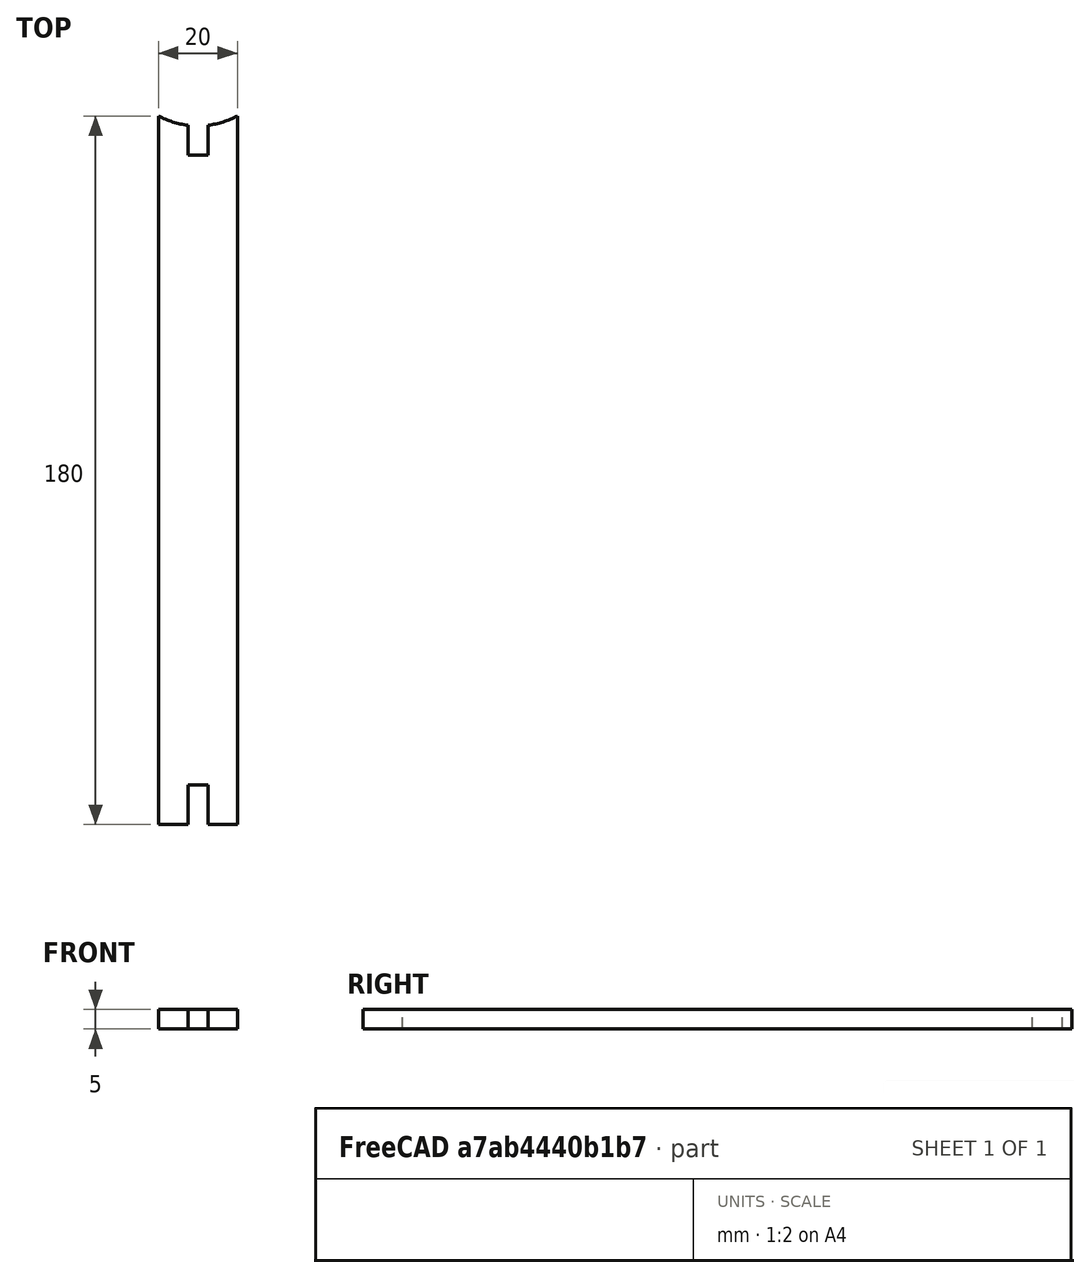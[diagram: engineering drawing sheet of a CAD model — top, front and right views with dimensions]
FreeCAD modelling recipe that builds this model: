
FCSTD DOCUMENT  (FreeCAD 1.0R39319 (Git))
Label: High Ball Holder
License: All rights reserved
LicenseURL: https://en.wikipedia.org/wiki/All_rights_reserved
objects: PartDesign::CoordinateSystem×2, Sketcher::SketchObject×1, PartDesign::Pad×1, PartDesign::Body×1, App::Part×1
note: 8 computed .brp shape members not serialized (recipe doc carries the construction recipe); baked Part::Feature solids carry a one-line shape summary decoded from their .brp

FEATURE [Sketcher::SketchObject] Sketch
  ArcFitTolerance = 1e-06
  AttachmentSupport = -> [XY_Plane001]
  FullyConstrained = true
  MakeInternals = false
  MapMode = 5
  sketch-geometry (15):
    g0: LineSegment StartX=-10 StartY=0 StartZ=0 EndX=-2.55 EndY=0 EndZ=0
    g1: LineSegment StartX=-2.55 StartY=0 StartZ=0 EndX=-2.55 EndY=10 EndZ=0
    g2: LineSegment StartX=-2.55 StartY=10 StartZ=0 EndX=2.55 EndY=10 EndZ=0
    g3: LineSegment StartX=2.55 StartY=10 StartZ=0 EndX=2.55 EndY=0 EndZ=0
    g4: LineSegment StartX=2.55 StartY=0 StartZ=0 EndX=10 EndY=0 EndZ=0
    g5: LineSegment StartX=10 StartY=0 StartZ=0 EndX=10 EndY=180 EndZ=0
    g6: LineSegment StartX=-10 StartY=180 StartZ=0 EndX=-10 EndY=0 EndZ=0
    g7: ArcOfCircle CenterX=4.5e-15 CenterY=198.466 CenterZ=0 NormalX=0 NormalY=0 NormalZ=1 AngleXU=0 Radius=21 StartAngle=4.21607 EndAngle=4.59066
    g8: LineSegment [constr] StartX=-10 StartY=180 StartZ=0 EndX=10 EndY=180 EndZ=0
    g9: LineSegment StartX=-2.55 StartY=177.622 StartZ=0 EndX=-2.55 EndY=170 EndZ=0
    g10: LineSegment StartX=-2.55 StartY=170 StartZ=0 EndX=2.55 EndY=170 EndZ=0
    g11: LineSegment StartX=2.55 StartY=170 StartZ=0 EndX=2.55 EndY=177.622 EndZ=0
    g12: ArcOfCircle CenterX=4.5e-15 CenterY=198.466 CenterZ=0 NormalX=0 NormalY=0 NormalZ=1 AngleXU=0 Radius=21 StartAngle=4.83412 EndAngle=5.20871
    g13: GeomPoint [constr] X=-3e-16 Y=170 Z=0
    g14: GeomPoint [constr] X=0 Y=10 Z=0
  constraints (42):
    c: Horizontal(g0)
    c: Coincident(g0,g1)
    c: Vertical(g1)
    c: Coincident(g1,g2)
    c: Horizontal(g2)
    c: Coincident(g2,g3)
    c: Vertical(g3)
    c: Coincident(g3,g4)
    c: Horizontal(g4)
    c: Coincident(g4,g5)
    c: Vertical(g5)
    c: Coincident(g6,g0)
    c: Vertical(g6)
    c: Coincident(g7,g6)
    c: Coincident(g12,g5)
    c: Coincident(g8,g6)
    c: Coincident(g8,g5)
    c: Horizontal(g8)
    c: Vertical(g9)
    c: Coincident(g9,g10)
    c: Horizontal(g10)
    c: Coincident(g10,g11)
    c: PointOnObject(g11,g12)
    c: Vertical(g11)
    c: Equal(g7,g12)
    c: Coincident(g7,g9)
    c: PointOnObject(g12,g11)
    c: Coincident(g7,g12)
    c: Symmetric(g10,g10,g13)
    c: Symmetric(g2,g2,g14)
    c: Distance(g5,g6) = 20
    c: Distance(g10,g10) = 5.1
    c: DistanceX(g2,g2) = 5.1
    c: PointOnObject(g3,g0)
    c: Distance(g14,g5) = 10
    c: Distance(g8,g10) = 10
    c: Distance(g13,g5) = 10
    c: DistanceY(g3,g3) = 10
    c: Radius(g7) = 21
    c: DistanceY(g6,g6) = 180
    c: PointOnObject(g14,g-2)
    c: PointOnObject(g0,g-1)
FEATURE [PartDesign::Pad] Pad
  Direction = (0,0,1)
  Length = 5
  Length2 = 10
  Midplane = true
  Profile = -> Sketch
  ReferenceAxis = -> Sketch [N_Axis]
  Refine = true
  Suppressed = false
  Type = 0
FEATURE [PartDesign::Body] Body  label="High Ball Holder001"
  AllowCompound = false
  Group = -> [Sketch,Pad]
  Origin = -> Origin001
  Tip = -> Pad
FEATURE [PartDesign::CoordinateSystem] LCS_1
  AttacherType = Attacher::AttachEngine3D
  AttachmentOffset = pos=(0,10,0) rot=(0,0,1;0rad)
  AttachmentSupport = -> [XY_Plane]
  MapMode = 2
  Placement = pos=(0,10,0) rot=(0,0,1;0rad)
FEATURE [PartDesign::CoordinateSystem] LCS_2
  AttacherType = Attacher::AttachEngine3D
  AttachmentOffset = pos=(0,170,0) rot=(0,0,1;0rad)
  AttachmentSupport = -> [XY_Plane]
  MapMode = 2
  Placement = pos=(0,170,0) rot=(0,0,1;0rad)
FEATURE [App::Part] Part  label="High Ball Holder"
  Group = -> [Body,LCS_1,LCS_2]
  Origin = -> Origin
